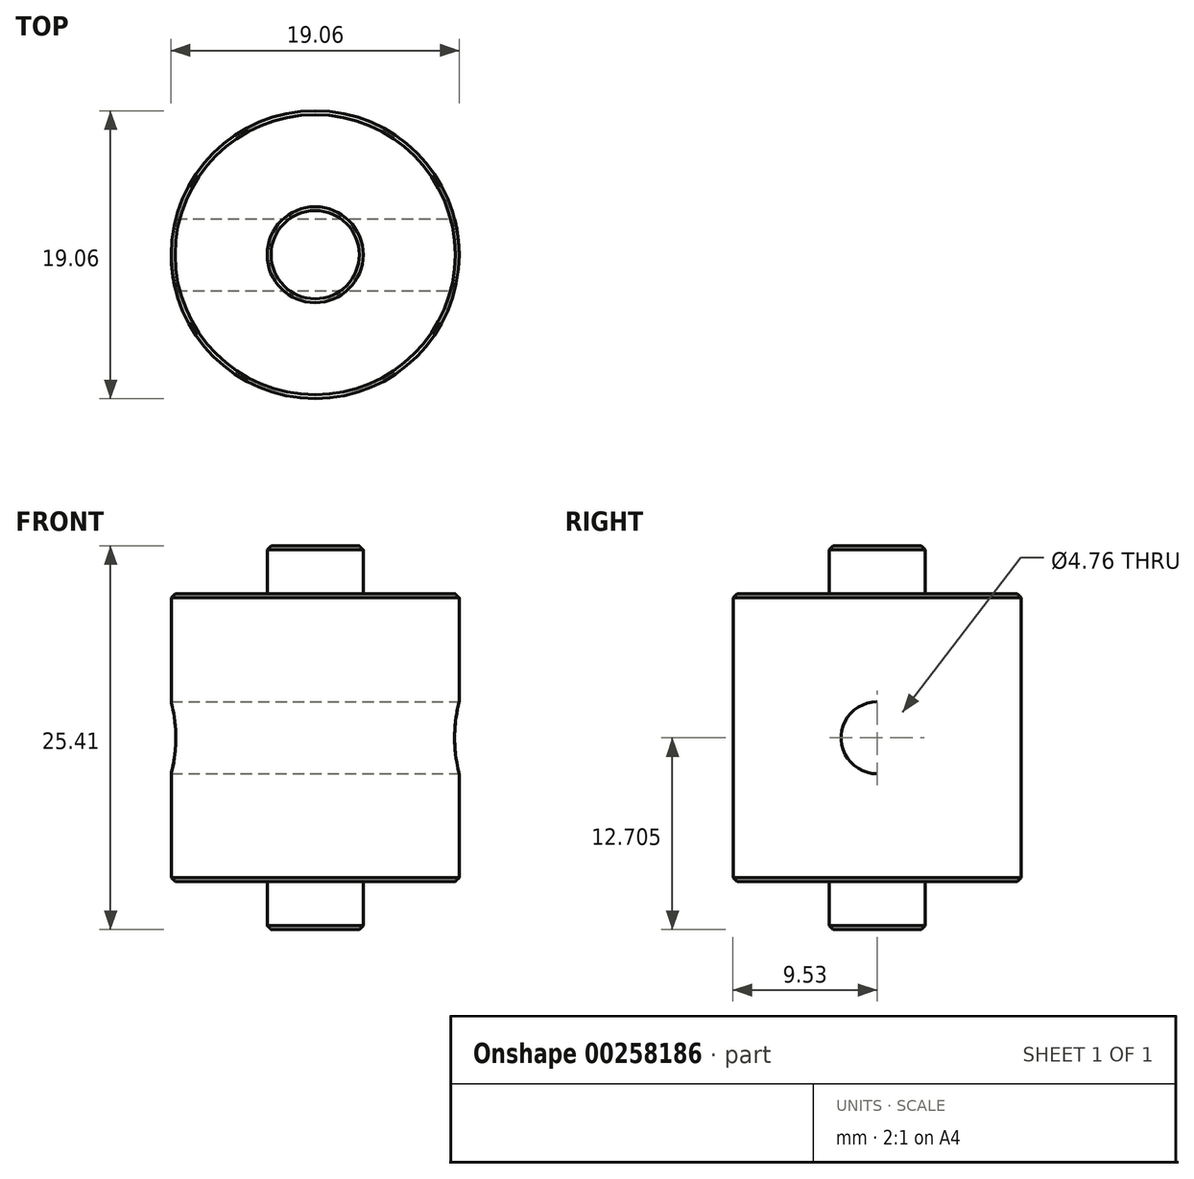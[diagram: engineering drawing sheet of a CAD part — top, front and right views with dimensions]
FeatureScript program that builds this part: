
annotation { "Feature Type Name" : "Feature", "Feature Type Description" : "" }
export const myFeature = defineFeature(function(context is Context, id is Id, definition is map)
    precondition{}
    {
        {
            var Q0;
            Q0=qCreatedBy(makeId("Top.planeOp"),FACE);
            var sketch = newSketch(context, id + "F0", { "sketchPlane" : qUnion([Q0])});
            skCircle(sketch, "E0", {"center": v(0, 0) * mm, "radius": 9.52 * mm});
            skSolve(sketch);
        }
        {
            var Q0;
            Q0 = qSketchRegion(id + "F0", true);
            extrude(context, id + "F1", {"entities" : qUnion([Q0]), "depth" : 19.05 * mm});
        }
        {
            var Q0;
            Q0=makeQuery(id+"F1.opExtrude","CAP_FACE",FACE,{"disambiguationData":[OSD([sQuery(id+"F0.wireOp",EDGE,"E0")])],"isStart":false});
            var sketch = newSketch(context, id + "F2", { "sketchPlane" : qUnion([Q0])});
            skCircle(sketch, "E1", {"center": v(0, 0) * mm, "radius": 3.18 * mm});
            skSolve(sketch);
        }
        {
            var Q0;
            Q0 = qSketchRegion(id + "F2", true);
            extrude(context, id + "F3", {"entities" : qUnion([Q0]), "operationType" : NewBodyOperationType.ADD, "depth" : 3.17 * mm});
        }
        {
            var Q0;
            Q0=makeQuery(id+"F1.opExtrude","CAP_FACE",FACE,{"disambiguationData":[OSD([sQuery(id+"F0.wireOp",EDGE,"E0")])],"isStart":true});
            var sketch = newSketch(context, id + "F4", { "sketchPlane" : qUnion([Q0])});
            skCircle(sketch, "E2", {"center": v(0, 0) * mm, "radius": 3.18 * mm});
            skSolve(sketch);
        }
        {
            var Q0;
            Q0 = qSketchRegion(id + "F4", true);
            extrude(context, id + "F5", {"entities" : qUnion([Q0]), "operationType" : NewBodyOperationType.ADD, "depth" : 3.17 * mm});
        }
        {
            var Q0;
            Q0=makeQuery(id+"F1.opExtrude","CAP_EDGE",EDGE,{"disambiguationData":[OSD([sQuery(id+"F0.wireOp",EDGE,"E0")])],"isStart":false});
            var Q1;
            Q1=makeQuery(id+"F3.opExtrude","CAP_EDGE",EDGE,{"disambiguationData":[OSD([sQuery(id+"F2.wireOp",EDGE,"E1")])],"isStart":false});
            var Q2;
            Q2=makeQuery(id+"F1.opExtrude","CAP_EDGE",EDGE,{"disambiguationData":[OSD([sQuery(id+"F0.wireOp",EDGE,"E0")])],"isStart":true});
            var Q3;
            Q3=makeQuery(id+"F5.opExtrude","CAP_EDGE",EDGE,{"disambiguationData":[OSD([sQuery(id+"F4.wireOp",EDGE,"E2")])],"isStart":false});
            chamfer(context, id + "F6", {"entities" : qUnion([Q0, Q1, Q2, Q3]), "width" : 0.25 * mm, "tangentPropagation" : true});
        }
        {
            var Q0;
            Q0=qCreatedBy(makeId("Right.planeOp"),FACE);
            var sketch = newSketch(context, id + "F7", { "sketchPlane" : qUnion([Q0])});
            skLineSegment(sketch, "E3", {"start": v(-9.52, 0.25) * mm, "end": v(-9.52, 18.8) * mm, "construction": true});
            skLineSegment(sketch, "E4", {"start": v(9.52, 18.8) * mm, "end": v(9.52, 0.25) * mm, "construction": true});
            skLineSegment(sketch, "E5", {"start": v(9.52, 18.8) * mm, "end": v(9.52, 0.25) * mm});
            skLineSegment(sketch, "E6", {"start": v(-9.52, 0.25) * mm, "end": v(-9.52, 18.8) * mm});
            skLineSegment(sketch, "E7", {"start": v(-9.52, 18.8) * mm, "end": v(9.52, 0.25) * mm, "construction": true});
            skCircle(sketch, "E8", {"center": v(0, 9.53) * mm, "radius": 2.38 * mm});
            skSolve(sketch);
        }
        {
            var Q0;
            Q0 = qSketchRegion(id + "F7", true);
            extrude(context, id + "F8", {"entities" : qUnion([Q0]), "operationType" : NewBodyOperationType.REMOVE, "endBound" : BoundingType.SYMMETRIC, "oppositeDirection" : true, "depth" : 25.4 * mm});
        }
    });
